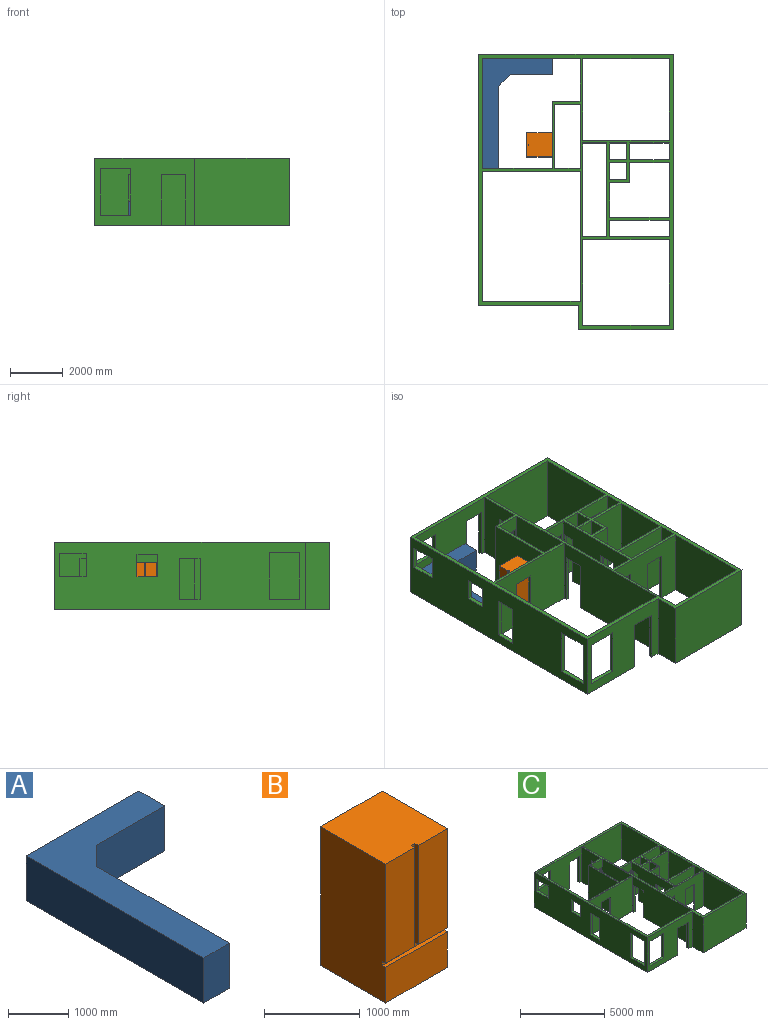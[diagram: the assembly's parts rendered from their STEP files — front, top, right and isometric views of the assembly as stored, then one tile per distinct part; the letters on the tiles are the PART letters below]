
ASSEMBLY  parts=3 mates=3
PART A: 9 faces, bbox 2641.6x4165.6x914.4 mm
  f0: plane 914.4x609.6mm, normal (0,-1,0), area 557418.2mm2, adj f1,f6,f7,f8
  f1: plane 3124.2x914.4mm, normal (1,0,0), area 2856768.5mm2, adj f0,f2,f7,f8
  f2: plane 914.4x431.8mm, normal (0.71,-0.71,0), area 558385.1mm2, adj f1,f3,f7,f8
  f3: plane 1600.2x914.4mm, normal (0,-1,0), area 1463222.9mm2, adj f2,f4,f7,f8
  f4: plane 914.4x609.6mm, normal (1,0,0), area 557418.2mm2, adj f3,f5,f7,f8
  f5: plane 2641.6x914.4mm, normal (0,1,0), area 2415479mm2, adj f4,f6,f7,f8
  f6: plane 4165.6x914.4mm, normal (-1,0,0), area 3809024.6mm2, adj f0,f5,f7,f8
  f7: plane 4165.6x2641.6mm, normal (0,0,1), area 3871282.6mm2, adj f0,f1,f2,f3,f4,f5,f6
  f8: plane 4165.6x2641.6mm, normal (0,0,-1), area 3871282.6mm2, adj f0,f1,f2,f3,f4,f5,f6
PART B: 14 faces, bbox 914.4x965.2x1778 mm
  f0: plane 1320.8x914.4mm, normal (0,-1,0), area 110967.5mm2, adj f1,f3,f4,f6,f8,f9,f11,f12
  f1: plane 1778x965.2mm, normal (1,0,0), area 1713545mm2, adj f0,f2,f4,f5,f6,f7,f11,f13
  f2: plane 1778x914.4mm, normal (0,1,0), area 1625803.2mm2, adj f1,f3,f4,f5
  f3: plane 1778x965.2mm, normal (-1,0,0), area 1713545mm2, adj f0,f2,f4,f5,f6,f7,f8,f10
  f4: plane 965.2x914.4mm, normal (0,0,1), area 879998.2mm2, adj f0,f1,f2,f3,f9,f10,f12,f13
  f5: plane 965.2x914.4mm, normal (0,0,-1), area 882578.9mm2, adj f1,f2,f3,f7
  f6: plane 914.4x50.8mm, normal (0,0,1), area 46451.5mm2, adj f0,f1,f3,f7
  f7: plane 914.4x457.2mm, normal (0,-1,0), area 418063.7mm2, adj f1,f3,f5,f6
  f8: plane 431.8x50.8mm, normal (0,0,-1), area 21935.4mm2, adj f0,f3,f9,f10
  f9: plane 1270x50.8mm, normal (1,0,0), area 64516mm2, adj f0,f4,f8,f10
  f10: plane 1270x431.8mm, normal (0,-1,0), area 548386mm2, adj f3,f4,f8,f9
  f11: plane 431.8x50.8mm, normal (0,0,-1), area 21935.4mm2, adj f0,f1,f12,f13
  f12: plane 1270x50.8mm, normal (-1,0,0), area 64516mm2, adj f0,f4,f11,f13
  f13: plane 1270x431.8mm, normal (0,-1,0), area 548386mm2, adj f1,f4,f11,f12
PART C: 121 faces, bbox 7366x10414x2540 mm
  f0: plane 4927.6x2540mm, normal (1,0,0), area 9248968.6mm2, adj f2,f53,f56,f57,f101,f102,f103,f104
  f1: plane 9499.6x2540mm, normal (-1,0,0), area 19342496.8mm2, adj f3,f5,f56,f57,f101,f102,f103,f104
  f2: plane 3683x2540mm, normal (0,1,0), area 5557408.2mm2, adj f0,f4,f43,f56,f57,f91,f92,f93
  f3: plane 3784.6x2540mm, normal (0,-1,0), area 5815472.2mm2, adj f1,f4,f54,f56,f57,f91,f92,f93
  f4: plane 10414x3911.6mm, normal (0,0,-1), area 4547732.8mm2, adj f2,f3,f5,f6,f7,f8,f9,f11
  f5: plane 7366x2540mm, normal (0,1,0), area 16259967.5mm2, adj f1,f4,f45,f56,f57,f94,f95,f96
  f6: plane 2540x1498.6mm, normal (0,-1,0), area 2335479.2mm2, adj f4,f33,f34,f56,f85,f86,f87
  f7: plane 3556x2540mm, normal (-1,0,0), area 6801276.7mm2, adj f4,f23,f25,f56,f76,f77,f78,f82
  f8: plane 2540x635mm, normal (1,0,0), area 754837.2mm2, adj f4,f46,f48,f56,f82,f83,f84
  f9: plane 2540x660.4mm, normal (0,1,0), area 819353.2mm2, adj f4,f40,f42,f56,f79,f80,f81
  f10: plane 2540x948.69mm, normal (0,-1,0), area 938707.9mm2, adj f12,f27,f50,f56,f73,f74,f75
  f11: plane 3098.8x2540mm, normal (1,0,0), area 6498051.5mm2, adj f4,f12,f13,f21,f56,f70,f71,f72
  f12: plane 2870.2x1981.2mm, normal (0,0,-1), area 759611.4mm2, adj f10,f11,f13,f14,f24,f25,f26,f27
  f13: plane 3276.6x2540mm, normal (0,1,0), area 5380634.4mm2, adj f4,f11,f12,f22,f56,f67,f68,f69
  f14: plane 2632.71x2540mm, normal (0,1,0), area 5216118.5mm2, adj f12,f28,f32,f56,f57,f58,f59,f60
  f15: plane 3251.2x2540mm, normal (-1,0,0), area 8258048mm2, adj f4,f16,f55,f56
  f16: plane 3276.6x2540mm, normal (0,1,0), area 8322564mm2, adj f4,f15,f17,f56
  f17: plane 3251.2x2540mm, normal (1,0,0), area 8258048mm2, adj f4,f16,f55,f56
  f18: plane 2540x2260.6mm, normal (0,-1,0), area 5741924mm2, adj f4,f19,f49,f56
  f19: plane 2540x635mm, normal (-1,0,0), area 1612900mm2, adj f4,f18,f20,f56
  f20: plane 2540x2260.6mm, normal (0,1,0), area 4270959.2mm2, adj f4,f19,f49,f56,f88,f89,f90
  f21: plane 3276.6x2540mm, normal (0,-1,0), area 8322564mm2, adj f4,f11,f22,f56
  f22: plane 3098.8x2540mm, normal (-1,0,0), area 7870952mm2, adj f4,f13,f21,f56
  f23: plane 2540x914.4mm, normal (0,1,0), area 851611.2mm2, adj f4,f7,f24,f56,f64,f65,f66
  f24: plane 3556x2540mm, normal (1,0,0), area 7561275.2mm2, adj f4,f12,f23,f25,f56,f61,f62,f63
  f25: plane 2540x914.4mm, normal (0,-1,0), area 851611.2mm2, adj f4,f7,f12,f24,f56,f67,f68,f69
  f26: plane 2540x948.69mm, normal (0,1,0), area 2409672.7mm2, adj f12,f27,f50,f56
  f27: plane 2540x2438.4mm, normal (1,0,0), area 6193536mm2, adj f10,f12,f26,f56
  f28: plane 4165.6x2540mm, normal (1,0,0), area 9061272.2mm2, adj f14,f29,f56,f57,f109,f110,f111,f112
  f29: plane 3683x2540mm, normal (0,-1,0), area 6905147.5mm2, adj f4,f28,f30,f56,f57,f94,f95,f96
  f30: plane 2540x1625.6mm, normal (-1,0,0), area 2756123.5mm2, adj f4,f12,f29,f31,f56,f70,f71,f72
  f31: plane 2540x1050.29mm, normal (0,1,0), area 1196771.9mm2, adj f12,f30,f32,f56,f73,f74,f75
  f32: plane 2540x2540mm, normal (-1,0,0), area 6451600mm2, adj f12,f14,f31,f56
  f33: plane 2540x635mm, normal (1,0,0), area 1612900mm2, adj f4,f6,f51,f56
  f34: plane 2540x635mm, normal (-1,0,0), area 1612900mm2, adj f4,f6,f51,f56
  f35: plane 2540x1498.6mm, normal (0,-1,0), area 3806444mm2, adj f4,f36,f52,f56
  f36: plane 2540x2082.8mm, normal (-1,0,0), area 5290312mm2, adj f4,f35,f37,f56
  f37: plane 2540x2260.6mm, normal (0,1,0), area 5741924mm2, adj f4,f36,f38,f56
  f38: plane 2540x1320.8mm, normal (1,0,0), area 1981931.5mm2, adj f4,f37,f39,f56,f76,f77,f78
  f39: plane 2540x762mm, normal (0,-1,0), area 1077417.2mm2, adj f4,f38,f52,f56,f79,f80,f81
  f40: plane 2540x660.4mm, normal (1,0,0), area 1677416mm2, adj f4,f9,f41,f56
  f41: plane 2540x660.4mm, normal (0,-1,0), area 1677416mm2, adj f4,f40,f42,f56
  f42: plane 2540x660.4mm, normal (-1,0,0), area 1677416mm2, adj f4,f9,f41,f56
  f43: plane 4927.6x2540mm, normal (-1,0,0), area 11045139.2mm2, adj f2,f4,f12,f53,f56,f61,f62,f63
  f44: plane 3581.4x2540mm, normal (0,-1,0), area 9096756mm2, adj f4,f45,f54,f56
  f45: plane 10414x2540mm, normal (1,0,0), area 26451560mm2, adj f4,f5,f44,f56
  f46: plane 2540x660.4mm, normal (0,-1,0), area 1677416mm2, adj f4,f8,f47,f56
  f47: plane 2540x635mm, normal (-1,0,0), area 1612900mm2, adj f4,f46,f48,f56
  f48: plane 2540x660.4mm, normal (0,1,0), area 1677416mm2, adj f4,f8,f47,f56
  f49: plane 2540x635mm, normal (1,0,0), area 1612900mm2, adj f4,f18,f20,f56
  f50: plane 2540x2438.4mm, normal (-1,0,0), area 6193536mm2, adj f10,f12,f26,f56
  f51: plane 2540x1498.6mm, normal (0,1,0), area 3806444mm2, adj f4,f33,f34,f56
  f52: plane 2540x762mm, normal (1,0,0), area 1935480mm2, adj f4,f35,f39,f56
  f53: plane 3683x2540mm, normal (0,-1,0), area 7883855.2mm2, adj f0,f12,f43,f56,f57,f58,f59,f60
  f54: plane 2540x914.4mm, normal (-1,0,0), area 2322576mm2, adj f3,f4,f44,f56
  f55: plane 3276.6x2540mm, normal (0,-1,0), area 5380634.4mm2, adj f4,f15,f17,f56,f64,f65,f66,f88
  f56: plane 10414x7366mm, normal (0,0,1), area 8684756.8mm2, adj f0,f1,f2,f3,f5,f6,f7,f8
  f57: plane 9499.6x2857.5mm, normal (0,0,-1), area 2337414.7mm2, adj f0,f1,f2,f3,f5,f14,f28,f29
  f58: plane 1930.4x101.6mm, normal (1,0,0), area 196128.6mm2, adj f14,f53,f57,f60
  f59: plane 1930.4x101.6mm, normal (-1,0,0), area 196128.6mm2, adj f12,f14,f53,f60
  f60: plane 762x101.6mm, normal (0,0,-1), area 77419.2mm2, adj f14,f53,f58,f59
  f61: plane 762x101.6mm, normal (0,0,-1), area 77419.2mm2, adj f24,f43,f62,f63
  f62: plane 1930.4x101.6mm, normal (0,1,0), area 196128.6mm2, adj f4,f24,f43,f61
  f63: plane 1930.4x101.6mm, normal (0,-1,0), area 196128.6mm2, adj f12,f24,f43,f61
  f64: plane 762x101.6mm, normal (0,0,-1), area 77419.2mm2, adj f23,f55,f65,f66
  f65: plane 1930.4x101.6mm, normal (-1,0,0), area 196128.6mm2, adj f4,f23,f55,f64
  f66: plane 1930.4x101.6mm, normal (1,0,0), area 196128.6mm2, adj f4,f23,f55,f64
  f67: plane 762x101.6mm, normal (0,0,-1), area 77419.2mm2, adj f13,f25,f68,f69
  f68: plane 1930.4x101.6mm, normal (1,0,0), area 196128.6mm2, adj f12,f13,f25,f67
  f69: plane 1930.4x101.6mm, normal (-1,0,0), area 196128.6mm2, adj f4,f13,f25,f67
  f70: plane 711.2x101.6mm, normal (0,0,-1), area 72257.9mm2, adj f11,f30,f71,f72
  f71: plane 1930.4x101.6mm, normal (0,-1,0), area 196128.6mm2, adj f4,f11,f30,f70
  f72: plane 1930.4x101.6mm, normal (0,1,0), area 196128.6mm2, adj f11,f12,f30,f70
  f73: plane 1930.4x101.6mm, normal (-1,0,0), area 196128.6mm2, adj f10,f12,f31,f75
  f74: plane 1930.4x101.6mm, normal (1,0,0), area 196128.6mm2, adj f10,f12,f31,f75
  f75: plane 762x101.6mm, normal (0,0,-1), area 77419.2mm2, adj f10,f31,f73,f74
  f76: plane 1930.4x101.6mm, normal (0,1,0), area 196128.6mm2, adj f4,f7,f38,f77
  f77: plane 711.2x101.6mm, normal (0,0,-1), area 72257.9mm2, adj f7,f38,f76,f78
  f78: plane 1930.4x101.6mm, normal (0,-1,0), area 196128.6mm2, adj f4,f7,f38,f77
  f79: plane 1930.4x101.6mm, normal (1,0,0), area 196128.6mm2, adj f4,f9,f39,f81
  f80: plane 1930.4x101.6mm, normal (-1,0,0), area 196128.6mm2, adj f4,f9,f39,f81
  f81: plane 444.5x101.6mm, normal (0,0,-1), area 45161.2mm2, adj f9,f39,f79,f80
  f82: plane 1930.4x101.6mm, normal (0,-1,0), area 196128.6mm2, adj f4,f7,f8,f84
  f83: plane 1930.4x101.6mm, normal (0,1,0), area 196128.6mm2, adj f4,f7,f8,f84
  f84: plane 444.5x101.6mm, normal (0,0,-1), area 45161.2mm2, adj f7,f8,f82,f83
  f85: plane 1930.4x101.6mm, normal (-1,0,0), area 196128.6mm2, adj f4,f6,f13,f87
  f86: plane 1930.4x101.6mm, normal (1,0,0), area 196128.6mm2, adj f4,f6,f13,f87
  f87: plane 762x101.6mm, normal (0,0,-1), area 77419.2mm2, adj f6,f13,f85,f86
  f88: plane 762x101.6mm, normal (0,0,-1), area 77419.2mm2, adj f20,f55,f89,f90
  f89: plane 1930.4x101.6mm, normal (-1,0,0), area 196128.6mm2, adj f4,f20,f55,f88
  f90: plane 1930.4x101.6mm, normal (1,0,0), area 196128.6mm2, adj f4,f20,f55,f88
  f91: plane 1930.4x152.4mm, normal (-1,0,0), area 294193mm2, adj f2,f3,f4,f93
  f92: plane 1930.4x152.4mm, normal (1,0,0), area 294193mm2, adj f2,f3,f57,f93
  f93: plane 914.4x152.4mm, normal (0,0,-1), area 139354.6mm2, adj f2,f3,f91,f92
  f94: plane 1930.4x152.4mm, normal (-1,0,0), area 294193mm2, adj f4,f5,f29,f95
  f95: plane 812.8x152.4mm, normal (0,0,-1), area 123870.7mm2, adj f5,f29,f94,f96
  f96: plane 1930.4x152.4mm, normal (1,0,0), area 294193mm2, adj f5,f29,f57,f95
  f97: plane 1143x152.4mm, normal (0,0,-1), area 174193.2mm2, adj f2,f3,f98,f100
  f98: plane 1778x152.4mm, normal (1,0,0), area 270967.2mm2, adj f2,f3,f97,f99
  f99: plane 1143x152.4mm, normal (0,0,1), area 174193.2mm2, adj f2,f3,f98,f100
  f100: plane 1778x152.4mm, normal (-1,0,0), area 270967.2mm2, adj f2,f3,f97,f99
  f101: plane 1143x152.4mm, normal (0,0,1), area 174193.2mm2, adj f0,f1,f102,f104
  f102: plane 1778x152.4mm, normal (0,1,0), area 270967.2mm2, adj f0,f1,f101,f103
  f103: plane 1143x152.4mm, normal (0,0,-1), area 174193.2mm2, adj f0,f1,f102,f104
  f104: plane 1778x152.4mm, normal (0,-1,0), area 270967.2mm2, adj f0,f1,f101,f103
  f105: plane 1568.3x152.4mm, normal (0,-1,0), area 239009.3mm2, adj f0,f1,f106,f107
  f106: plane 787.4x152.4mm, normal (0,0,1), area 119999.8mm2, adj f0,f1,f105,f108
  f107: plane 787.4x152.4mm, normal (0,0,-1), area 119999.8mm2, adj f0,f1,f105,f108
  f108: plane 1568.3x152.4mm, normal (0,1,0), area 239009.3mm2, adj f0,f1,f106,f107
  f109: plane 990.6x152.4mm, normal (0,0,-1), area 150967.4mm2, adj f1,f28,f110,f111
  f110: plane 889x152.4mm, normal (0,-1,0), area 135483.6mm2, adj f1,f28,f109,f112
  f111: plane 889x152.4mm, normal (0,1,0), area 135483.6mm2, adj f1,f28,f109,f112
  f112: plane 990.6x152.4mm, normal (0,0,1), area 150967.4mm2, adj f1,f28,f110,f111
  f113: plane 889x152.4mm, normal (1,0,0), area 135483.6mm2, adj f5,f29,f114,f115
  f114: plane 990.6x152.4mm, normal (0,0,-1), area 150967.4mm2, adj f5,f29,f113,f116
  f115: plane 990.6x152.4mm, normal (0,0,1), area 150967.4mm2, adj f5,f29,f113,f116
  f116: plane 889x152.4mm, normal (-1,0,0), area 135483.6mm2, adj f5,f29,f114,f115
  f117: plane 838.2x152.4mm, normal (0,1,0), area 127741.7mm2, adj f1,f28,f118,f119
  f118: plane 762x152.4mm, normal (0,0,-1), area 116128.8mm2, adj f1,f28,f117,f120
  f119: plane 762x152.4mm, normal (0,0,1), area 116128.8mm2, adj f1,f28,f117,f120
  f120: plane 838.2x152.4mm, normal (0,-1,0), area 127741.7mm2, adj f1,f28,f118,f119
PLACE A t=(13620.92,-2618.7,-160.39)mm
PLACE B rot(axis=(0,0,-1),90deg) t=(8314.07,4730,-158.21)mm
PLACE C t=(13620.92,-2618.7,-156.88)mm
MATE planar C.f28 <-> A.f6  axis (1,0,0) through (6559.72,5482.48,1044.63)mm
MATE planar B.f2 <-> C.f32  axis (1,0,0) through (9192.43,4353.8,730.79)mm
MATE planar A.f5 <-> C.f29  axis (0,1,0) through (7880.52,7625.11,296.81)mm
